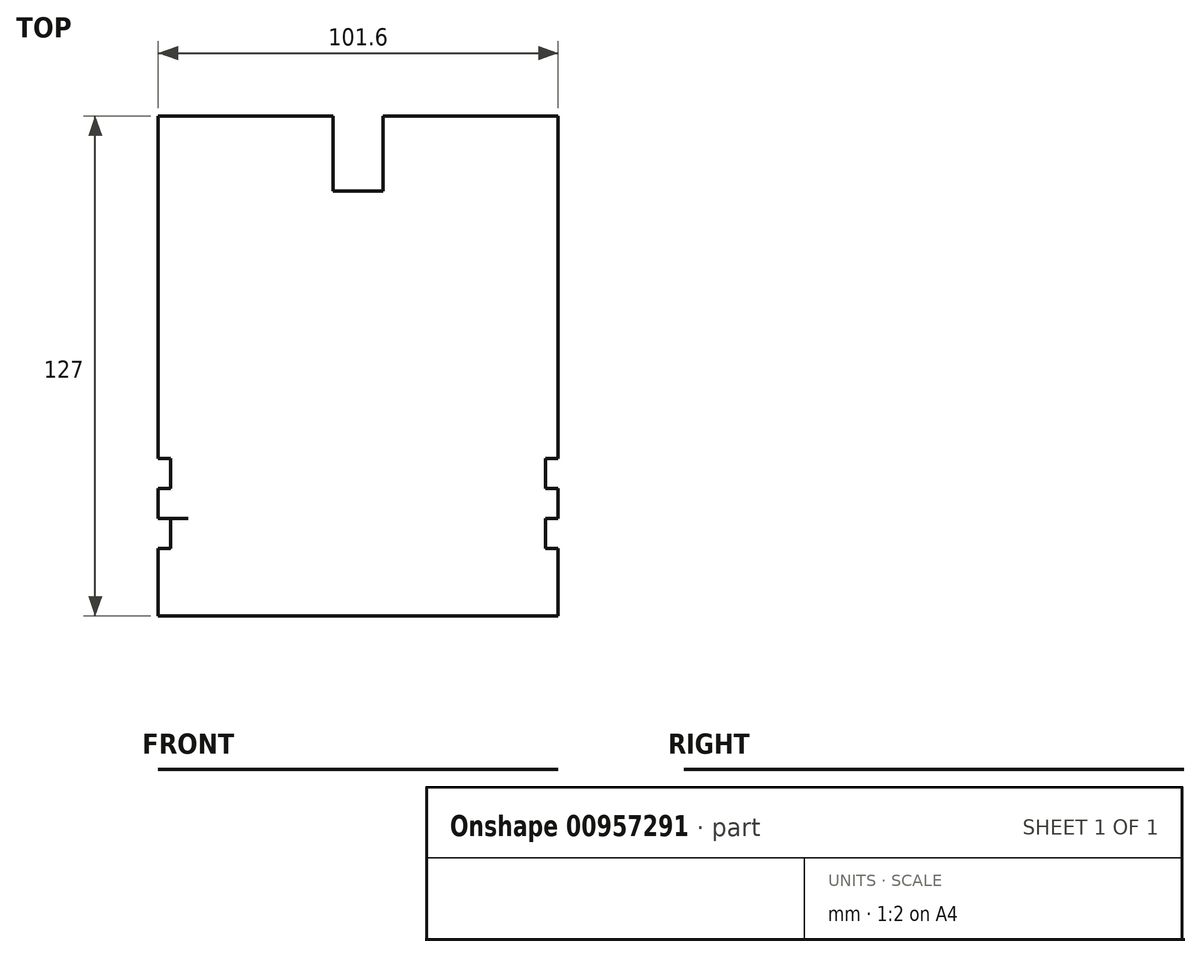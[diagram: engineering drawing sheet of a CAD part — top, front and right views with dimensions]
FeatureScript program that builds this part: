
annotation { "Feature Type Name" : "Feature", "Feature Type Description" : "" }
export const myFeature = defineFeature(function(context is Context, id is Id, definition is map)
    precondition{}
    {
        {
            var Q0;
            Q0=qCreatedBy(makeId("Top.planeOp"),FACE);
            var sketch = newSketch(context, id + "F0", { "sketchPlane" : qUnion([Q0])});
            skLineSegment(sketch, "E0", {"start": v(0, 0) * mm, "end": v(101.6, 0) * mm});
            skLineSegment(sketch, "E1", {"start": v(101.6, 0) * mm, "end": v(101.6, 17.15) * mm});
            skLineSegment(sketch, "E2", {"start": v(101.6, 17.15) * mm, "end": v(93.98, 17.15) * mm});
            skLineSegment(sketch, "E3", {"start": v(93.98, 17.15) * mm, "end": v(93.98, 24.77) * mm});
            skLineSegment(sketch, "E4", {"start": v(93.98, 24.77) * mm, "end": v(101.6, 24.77) * mm});
            skLineSegment(sketch, "E5", {"start": v(93.98, 32.39) * mm, "end": v(101.6, 32.39) * mm});
            skLineSegment(sketch, "E6", {"start": v(101.6, 32.39) * mm, "end": v(101.6, 24.77) * mm});
            skLineSegment(sketch, "E7", {"start": v(93.98, 32.39) * mm, "end": v(93.98, 40) * mm});
            skLineSegment(sketch, "E8", {"start": v(93.98, 40) * mm, "end": v(101.6, 40) * mm});
            skLineSegment(sketch, "E9", {"start": v(101.6, 40) * mm, "end": v(101.6, 127) * mm});
            skLineSegment(sketch, "E10", {"start": v(0, 0) * mm, "end": v(0, 17.15) * mm});
            skLineSegment(sketch, "E11", {"start": v(0, 17.15) * mm, "end": v(7.62, 17.15) * mm});
            skLineSegment(sketch, "E12", {"start": v(7.62, 17.15) * mm, "end": v(7.62, 24.77) * mm});
            skLineSegment(sketch, "E13", {"start": v(7.62, 24.77) * mm, "end": v(0, 24.77) * mm});
            skLineSegment(sketch, "E14", {"start": v(0, 24.77) * mm, "end": v(0, 32.37) * mm});
            skLineSegment(sketch, "E15", {"start": v(0, 32.37) * mm, "end": v(7.62, 32.38) * mm});
            skLineSegment(sketch, "E16", {"start": v(7.62, 32.38) * mm, "end": v(7.6, 40) * mm});
            skLineSegment(sketch, "E17", {"start": v(7.6, 40) * mm, "end": v(0, 40) * mm});
            skLineSegment(sketch, "E18", {"start": v(0, 40) * mm, "end": v(0, 127) * mm});
            skLineSegment(sketch, "E19", {"start": v(57.15, 127) * mm, "end": v(57.15, 107.95) * mm});
            skLineSegment(sketch, "E20", {"start": v(44.45, 127) * mm, "end": v(44.45, 107.95) * mm});
            skLineSegment(sketch, "E21", {"start": v(44.45, 107.95) * mm, "end": v(57.15, 107.95) * mm});
            skLineSegment(sketch, "E22", {"start": v(44.45, 127) * mm, "end": v(0, 127) * mm});
            skLineSegment(sketch, "E23", {"start": v(57.15, 127) * mm, "end": v(101.6, 127) * mm});
            skPoint(sketch, "E24.orphan", {"position": v(50.8, 0) * mm});
            skSolve(sketch);
        }
        {
            var Q0;
            Q0=makeQuery(id+"F0.imprint","IMPRINT",FACE,{"disambiguationData":[TD([[makeQuery(id+"F0.imprint","IMPRINT",EDGE,{"derivedFrom":sQuery(id+"F0.wireOp",EDGE,"E0")}),1.0]])]});
            extrude(context, id + "F1", {"entities" : qUnion([Q0]), "depth" : 1 / 203.2 * mm, "offsetDistance" : 25.4 * mm});
        }
        {
            var Q0;
            Q0=makeQuery(id+"F1.opExtrude","SWEPT_FACE",FACE,{"disambiguationData":[OSD([sQuery(id+"F0.wireOp",EDGE,"E7")])]});
            var Q1;
            Q1=makeQuery(id+"F1.opExtrude","SWEPT_FACE",FACE,{"disambiguationData":[OSD([sQuery(id+"F0.wireOp",EDGE,"E3")])]});
            extrude(context, id + "F2", {"entities" : qUnion([Q0, Q1]), "operationType" : NewBodyOperationType.ADD, "depth" : 4.44 * mm, "offsetDistance" : 25.4 * mm});
        }
        {
            var Q0;
            Q0=makeQuery(id+"F1.opExtrude","SWEPT_FACE",FACE,{"disambiguationData":[OSD([sQuery(id+"F0.wireOp",EDGE,"E16")])]});
            var Q1;
            Q1=makeQuery(id+"F1.opExtrude","SWEPT_FACE",FACE,{"disambiguationData":[OSD([sQuery(id+"F0.wireOp",EDGE,"E12")])]});
            extrude(context, id + "F3", {"entities" : qUnion([Q0, Q1]), "operationType" : NewBodyOperationType.ADD, "depth" : 4.44 * mm, "offsetDistance" : 25.4 * mm});
        }
    });
